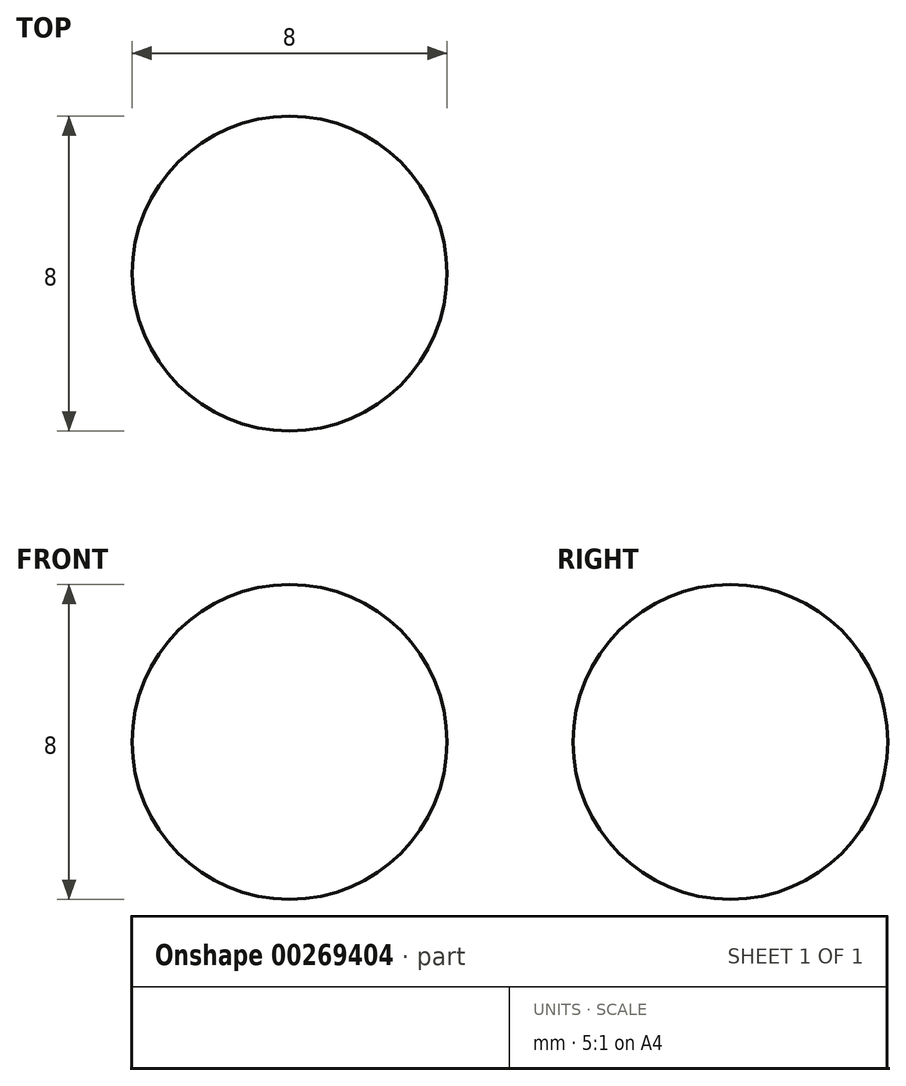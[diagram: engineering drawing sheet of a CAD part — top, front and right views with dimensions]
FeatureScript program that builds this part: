
annotation { "Feature Type Name" : "Feature", "Feature Type Description" : "" }
export const myFeature = defineFeature(function(context is Context, id is Id, definition is map)
    precondition{}
    {
        {
            var Q0;
            Q0=qCreatedBy(makeId("Top.planeOp"),FACE);
            var sketch = newSketch(context, id + "F0", { "sketchPlane" : qUnion([Q0])});
            skCircle(sketch, "E0", {"center": v(0, 0) * mm, "radius": 4 * mm});
            skSolve(sketch);
        }
        {
            var Q0;
            Q0=qCreatedBy(makeId("Front.planeOp"),FACE);
            var sketch = newSketch(context, id + "F1", { "sketchPlane" : qUnion([Q0])});
            skLineSegment(sketch, "E1", {"start": v(0, 4) * mm, "end": v(0, -4) * mm});
            skPoint(sketch, "E2", {"position": v(0, 0) * mm});
            skArc(sketch, "E3", {"start": v(0, -4) * mm, "mid": v(4, 0) * mm, "end": v(0, 4) * mm});
            skSolve(sketch);
        }
        {
            var Q0;
            Q0=makeQuery(id+"F1.imprint","IMPRINT",FACE,{"disambiguationData":[TD([[makeQuery(id+"F1.imprint","IMPRINT",EDGE,{"derivedFrom":sQuery(id+"F1.wireOp",EDGE,"E1")}),1.0]])]});
            var Q1;
            Q1=sQuery(id+"F0.wireOp",EDGE,"E0");
            revolve(context, id + "F2", {"entities" : qUnion([Q0]), "axis" : qUnion([Q1]), "revolveType" : RevolveType.FULL});
        }
    });
